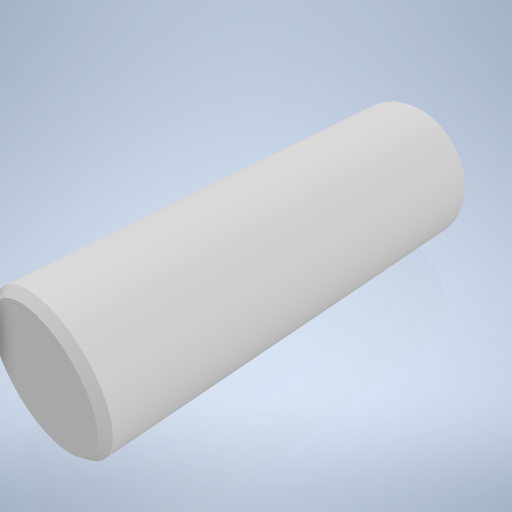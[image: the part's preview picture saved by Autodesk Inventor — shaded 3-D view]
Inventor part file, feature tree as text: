
AUTODESK INVENTOR PART (.ipt)
format: ipt  version: 2024.2 (Build 282272000, 272)  size: 211,456 bytes
history: native  units: mm
features: extrude x1, chamfer x1, sketch x1
ambient origin geometry x8: Origin, YZ Plane, XZ Plane, XY Plane, X Axis, Y Axis, Z Axis, Center Point
bodies: Volumenkörper1 (feature_tree)
feature tree (3):
  extrude  "Extrusion1"  Depth=6.0mm TaperAngle=0.0deg
  chamfer  "Fasen1"  Distance=0.1mm Angle=45.0deg
  sketch  "Skizze1"  dims[d0=2.0mm d1=6.0mm d2=0.0mm d3=0.1mm d4=2.0mm d5=45.0deg]
